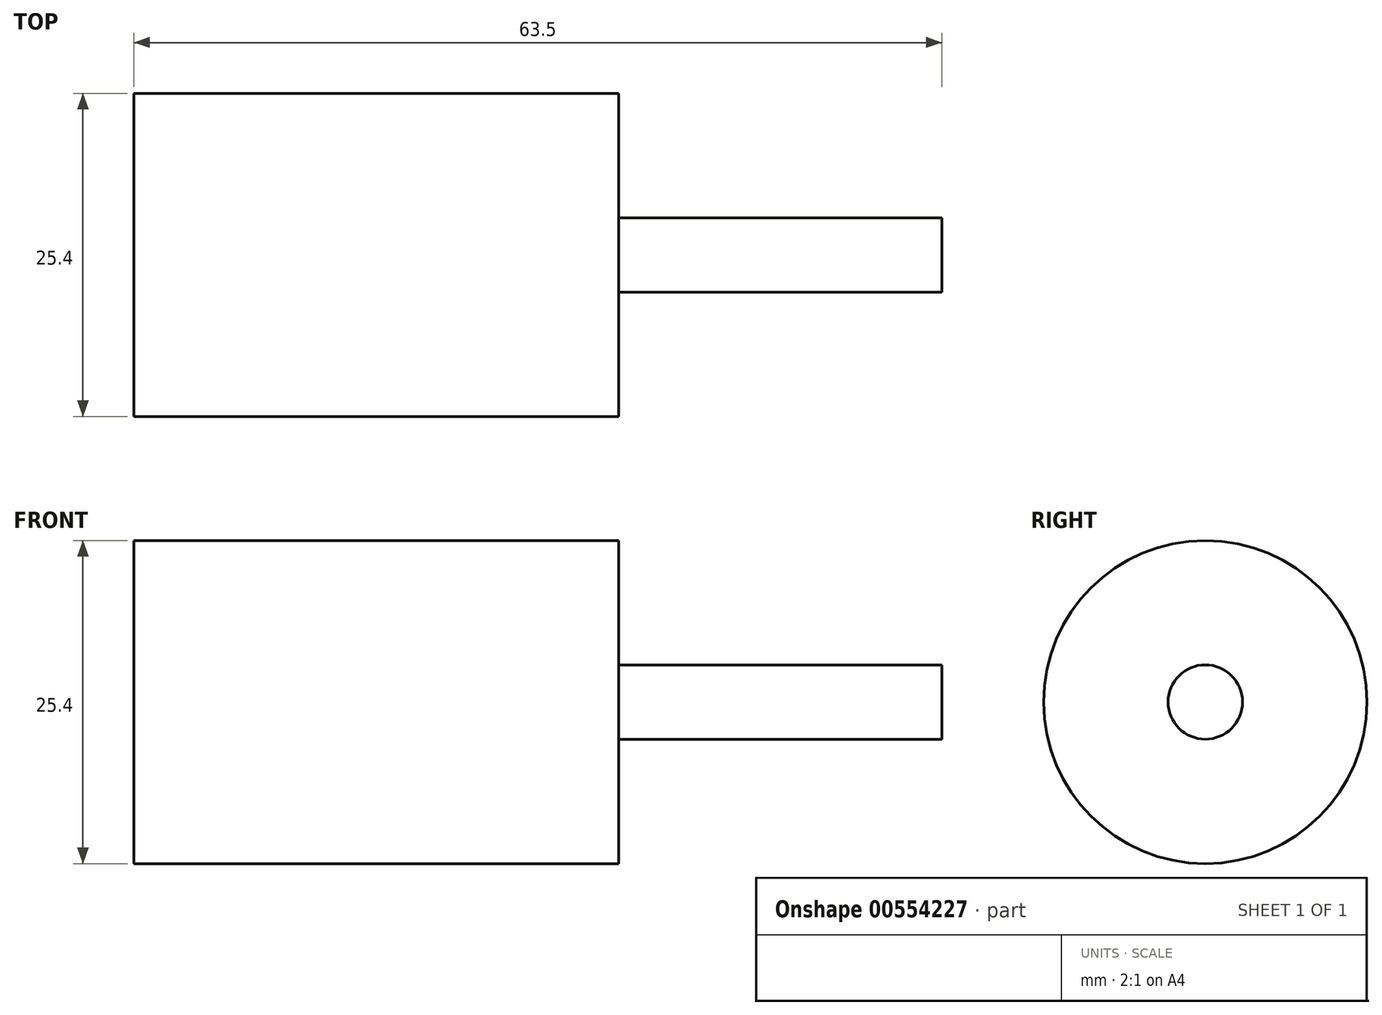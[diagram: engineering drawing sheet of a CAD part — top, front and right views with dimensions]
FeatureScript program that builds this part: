
annotation { "Feature Type Name" : "Feature", "Feature Type Description" : "" }
export const myFeature = defineFeature(function(context is Context, id is Id, definition is map)
    precondition{}
    {
        {
            var Q0;
            Q0=qCreatedBy(makeId("Right.planeOp"),FACE);
            var sketch = newSketch(context, id + "F0", { "sketchPlane" : qUnion([Q0])});
            skCircle(sketch, "E0", {"center": v(0, 0) * mm, "radius": 12.7 * mm});
            skSolve(sketch);
        }
        {
            var Q0;
            Q0 = qSketchRegion(id + "F0", true);
            extrude(context, id + "F1", {"entities" : qUnion([Q0]), "depth" : 38.1 * mm, "offsetDistance" : 25.4 * mm});
        }
        {
            var Q0;
            Q0=makeQuery(id+"F1.opExtrude","CAP_FACE",FACE,{"disambiguationData":[OSD([sQuery(id+"F0.wireOp",EDGE,"E0")])],"isStart":false});
            var sketch = newSketch(context, id + "F2", { "sketchPlane" : qUnion([Q0])});
            skCircle(sketch, "E1", {"center": v(0, 0) * mm, "radius": 2.92 * mm});
            skSolve(sketch);
        }
        {
            var Q0;
            Q0 = qSketchRegion(id + "F2", true);
            extrude(context, id + "F3", {"entities" : qUnion([Q0]), "operationType" : NewBodyOperationType.ADD, "depth" : 25.4 * mm, "offsetDistance" : 25.4 * mm});
        }
    });
